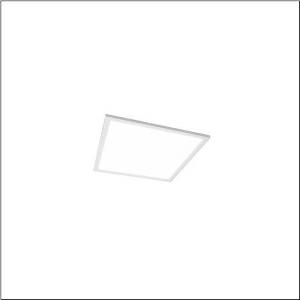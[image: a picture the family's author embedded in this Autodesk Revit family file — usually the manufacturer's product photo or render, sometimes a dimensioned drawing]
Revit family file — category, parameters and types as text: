
# Revit family: apollon_21_square_51mq13wd2313
name_source: partatom
category: Lighting Fixtures
units: mm (PartAtom-declared; Revit-internal decimal feet)

## family parameters
Cut with Voids When Loaded = No
Host = Face
Light Source = No
Part Type = Normal
Room Calculation Point = No
Round Connector Dimension = Use Diameter
Shared = No

## types (1)
- Apollon 21 square (1 x LED, 1700 lm, 15 W, 3000K)
    Apparent Load = 15 VA
    CIE Flux Codes = 59 88 97 100 100
    Color Rendering = 80
    Color Temperature = 3000K
    Default Elevation = 1800 mm
    Description = Apollon 21 square, office luminaire, primary optical cover: micro prismatic cover, of PMMA, light emission: direct distribution, primary light characteristic: symmetric, installation type: recessed, LED, rated luminous flux: 1.700lm, luminous efficacy: 115lm/W, light colour: 830, colour temperature: 3000K, control gear: DALI 2, with terminal, 5-pole, mains connection: 220..240V, AC/DC, 0/50..60Hz, rated input power: 15W, housing, of sheet steel, coated, traffic white (RAL 9016), with rapid mounting bracket, length: 296mm, width: 296mm, height: 40mm, housing upper side, of sheet steel, galvanised, protection rating (complete): IP20, protection rating (lamp compartment, on room side): IP50, insulation class (complete): insulation class II (safety insulation), certification: CE, ENEC, impact resistance: IK02, permissible operating ambient temperature: -20..+40°C, packaging unit: 1 piece
    Height = 0 mm  [stored 0 ft]
    Lamp = 1 x LED
    Lamp Light Flux = 1700 lm
    Lamp Power = 15 W
    Lamp count = 1
    Length = 295 mm
    Luminous efficacy = 113 lm/W
    Manufacturer = Siteco
    ModVariant = No
    Model = 51MQ13WD2313
    Mounting Place = Ceiling
    Mounting Type = Recessed
    Number of Poles = 1
    OnlyDefault = Yes
    Power Factor = 1
    Product Name = Apollon 21 square
    Product group = office luminaire | ceiling recessed
    ProductGroupID = 400
    Protection Class = Protection class II
    Protection Degree = IP 20
    RLX_Detail_Level = 1
    RLX_Emergency_Light_Flux = 0 lm
    RLX_Emergency_Type = 0
    RLX_Emergency_Type_DB = No
    RlxData = <blob elided: 9129 chars, md5=108c6039>
    Socket = socket
    Standby Power = 0 W
    System Light Flux = 1700 lm
    System Power = 15 W
    Type Comments = Product without accessories
    Type Image = l_1291030.jpg
    URL = http://relux.com
    VarID = ---
    Voltage = 0 V
    Weight = 0.00 kg
    Width = 295 mm

note: [stored X ft] marks values corroborated as IEEE doubles in the binary element streams (Revit-internal decimal feet)

## geometry (parser evidence)
native form markers: Sweep x10
no freeform markers — native parametric forms only
